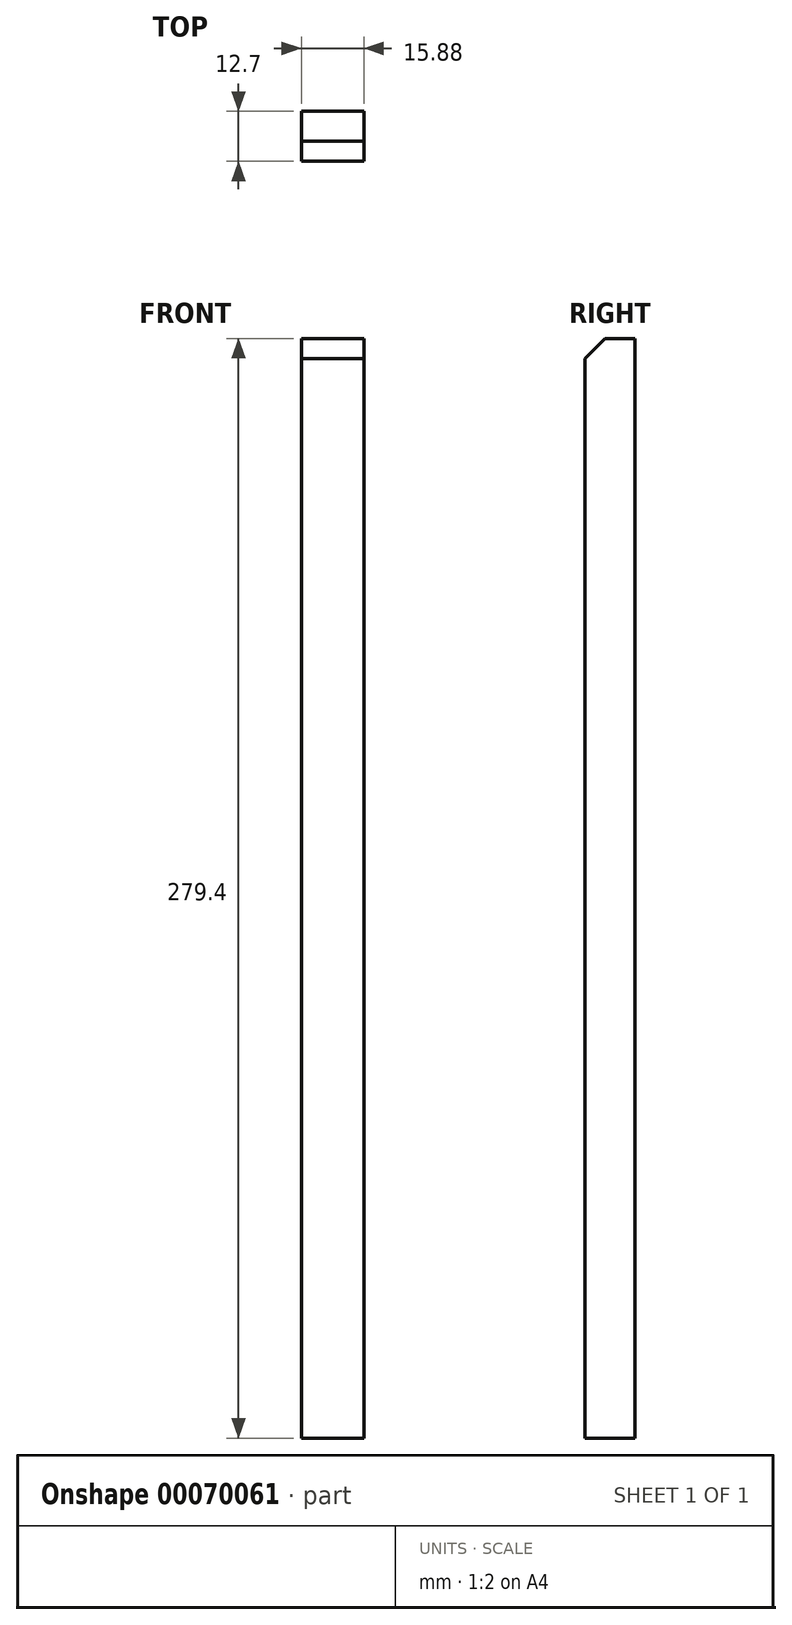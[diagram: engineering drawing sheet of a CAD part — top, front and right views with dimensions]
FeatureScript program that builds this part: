
annotation { "Feature Type Name" : "Feature", "Feature Type Description" : "" }
export const myFeature = defineFeature(function(context is Context, id is Id, definition is map)
    precondition{}
    {
        {
            var Q0;
            Q0=qCreatedBy(makeId("Top.planeOp"),FACE);
            var sketch = newSketch(context, id + "F0", { "sketchPlane" : qUnion([Q0])});
            skLineSegment(sketch, "E0.bottom", {"start": v(-7.94, 6.35) * mm, "end": v(7.94, 6.35) * mm});
            skLineSegment(sketch, "E0.top", {"start": v(-7.94, -6.35) * mm, "end": v(7.94, -6.35) * mm});
            skLineSegment(sketch, "E0.left", {"start": v(-7.94, 6.35) * mm, "end": v(-7.94, -6.35) * mm});
            skLineSegment(sketch, "E0.right", {"start": v(7.94, 6.35) * mm, "end": v(7.94, -6.35) * mm});
            skSolve(sketch);
        }
        {
            var Q0;
            Q0=makeQuery(id+"F0.imprint","IMPRINT",FACE,{"disambiguationData":[TD([[makeQuery(id+"F0.imprint","IMPRINT",EDGE,{"derivedFrom":sQuery(id+"F0.wireOp",EDGE,"E0.bottom")}),-1.0]])]});
            extrude(context, id + "F1", {"entities" : qUnion([Q0]), "depth" : 279.4 * mm});
        }
        {
            var Q0;
            Q0=makeQuery(id+"F1.opExtrude","CAP_EDGE",EDGE,{"disambiguationData":[OSD([sQuery(id+"F0.wireOp",EDGE,"E0.top")])],"isStart":false});
            chamfer(context, id + "F2", {"entities" : qUnion([Q0]), "width" : 5.08 * mm, "tangentPropagation" : true});
        }
    });
